# Revit family: Seating-Casual-Naughtone-Cloud_Plain_3_Booth
name_source: partatom
category: Furniture
revit_build: Autodesk Revit 2014 (Build: 20130709_2115(x64)
units: mm (PartAtom-declared; Revit-internal decimal feet)

## types (1)
- CLO-BOOTH-3
    Additional Materials = Additional material and finish options available. Please contact Naughtone direct for further information.
    AssetIdentifier = CLO-BOOTH-3
    Barcode = 0
    COBie Description = Designed by Naughtone, Cloud plain seating system's tactile, pillowy surround is designed to invite and comfort without consuming masses of space. Whether you are looking for somewhere to shelter or meet or simply to relax, cloud has a magnetic appeal.
    Cost = 0 $
    Current Revision = 1
    Depth = 2200 mm  [stored 7.21785 ft]
    Description = Cloud Booth Three Seat Sofa
    Height = 1300 mm  [stored 4.26509 ft]
    Length = 2100 mm  [stored 6.88976 ft]
    Manufacturer = Naughtone
    Model = Cloud Booth Three Seat Sofa
    Name = Furniture-Seating-Casual-Cloud_Plain
    Product Code = CLO-BOOTH-3
    Product URL = http://www.naughtone.com
    SerialNumber = 0
    TagNumber = 0
    TypeName = 2100mmx2200mm1300mm, Cloud Plain
    URL = http://www.naughtone.com
    Uniclass = Pr_40_50_12_81
    WarrantyDuration = 60

note: [stored X ft] marks values corroborated as IEEE doubles in the binary element streams (Revit-internal decimal feet)

## geometry (parser evidence)
native form markers: Blend x2, Sweep x13
no freeform markers — native parametric forms only
